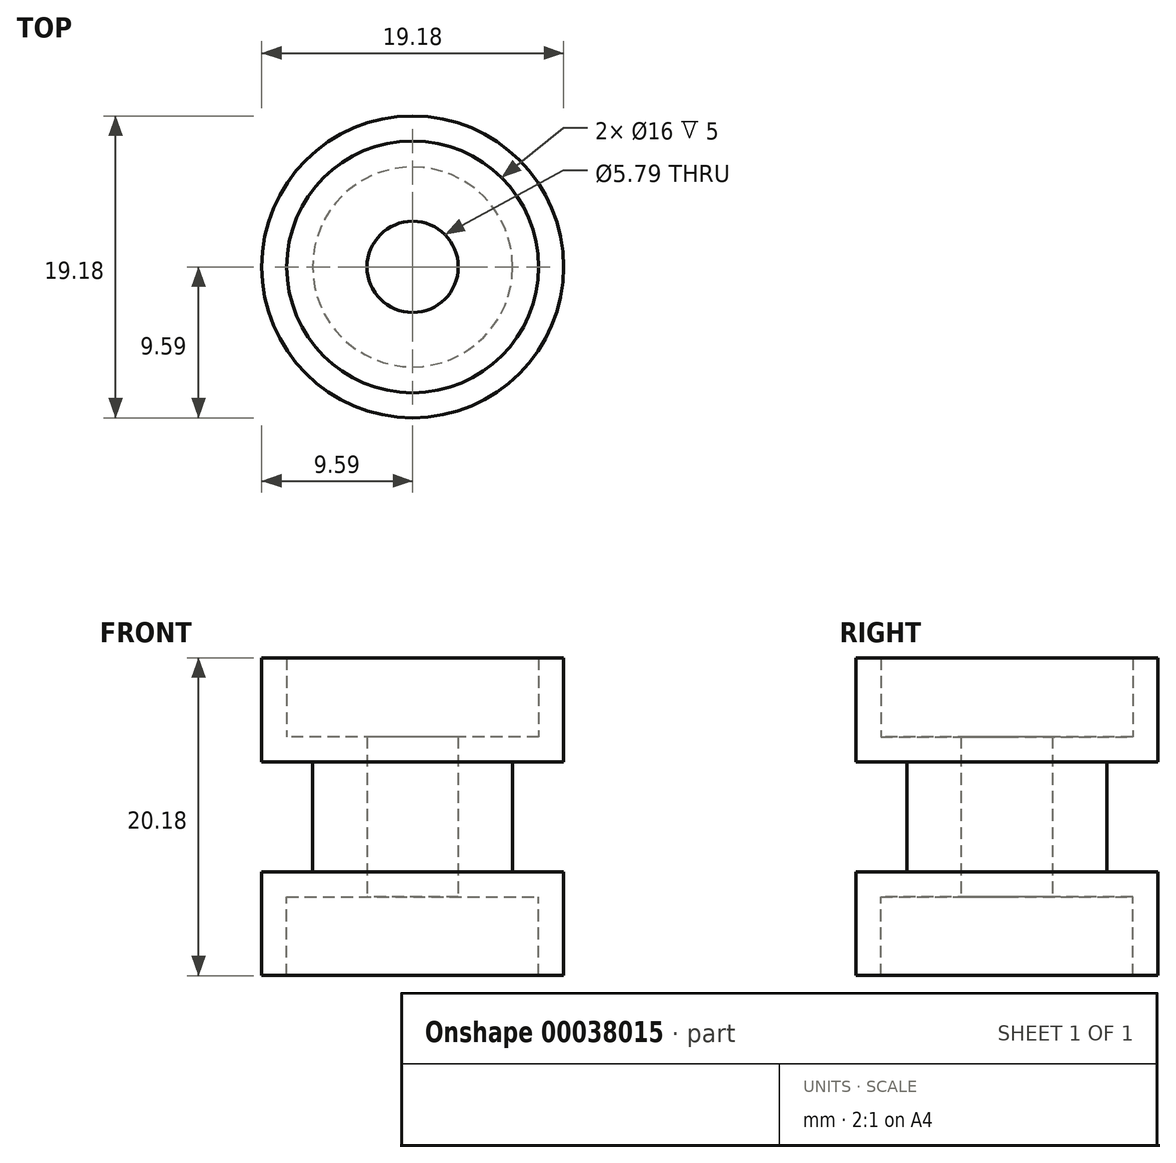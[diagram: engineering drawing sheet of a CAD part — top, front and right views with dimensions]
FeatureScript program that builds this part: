
annotation { "Feature Type Name" : "Feature", "Feature Type Description" : "" }
export const myFeature = defineFeature(function(context is Context, id is Id, definition is map)
    precondition{}
    {
        {
            var Q0;
            Q0=qCreatedBy(makeId("Top.planeOp"),FACE);
            var sketch = newSketch(context, id + "F0", { "sketchPlane" : qUnion([Q0])});
            skCircle(sketch, "E0", {"center": v(0, 0) * mm, "radius": 6.35 * mm});
            skCircle(sketch, "E1", {"center": v(0, 0) * mm, "radius": 2.9 * mm});
            skSolve(sketch);
        }
        {
            var Q0;
            Q0 = qSketchRegion(id + "F0", true);
            extrude(context, id + "F1", {"entities" : qUnion([Q0]), "depth" : 7 * mm});
        }
        {
            var Q0;
            Q0=makeQuery(id+"F1.opExtrude","CAP_FACE",FACE,{"disambiguationData":[OSD([sQuery(id+"F0.wireOp",EDGE,"E0"),sQuery(id+"F0.wireOp",EDGE,"E1")])],"isStart":false});
            var sketch = newSketch(context, id + "F2", { "sketchPlane" : qUnion([Q0])});
            skCircle(sketch, "E2", {"center": v(0, 0) * mm, "radius": 9.59 * mm});
            skCircle(sketch, "E3", {"center": v(0, 0) * mm, "radius": 2.9 * mm});
            skSolve(sketch);
        }
        {
            var Q0;
            Q0 = qSketchRegion(id + "F2", true);
            extrude(context, id + "F3", {"entities" : qUnion([Q0]), "operationType" : NewBodyOperationType.ADD, "depth" : 1.59 * mm});
        }
        {
            var Q0;
            Q0=makeQuery(id+"F3.opExtrude","CAP_FACE",FACE,{"disambiguationData":[OSD([sQuery(id+"F2.wireOp",EDGE,"E2"),sQuery(id+"F2.wireOp",EDGE,"E3")])],"isStart":false});
            var sketch = newSketch(context, id + "F4", { "sketchPlane" : qUnion([Q0])});
            skCircle(sketch, "E4", {"center": v(0, 0) * mm, "radius": 9.59 * mm});
            skCircle(sketch, "E5", {"center": v(0, 0) * mm, "radius": 8 * mm});
            skSolve(sketch);
        }
        {
            var Q0;
            Q0 = qSketchRegion(id + "F4", true);
            extrude(context, id + "F5", {"entities" : qUnion([Q0]), "operationType" : NewBodyOperationType.ADD, "depth" : 5 * mm});
        }
        {
            var Q0;
            Q0=makeQuery(id+"F1.opExtrude","CAP_FACE",FACE,{"disambiguationData":[OSD([sQuery(id+"F0.wireOp",EDGE,"E0"),sQuery(id+"F0.wireOp",EDGE,"E1")])],"isStart":true});
            var sketch = newSketch(context, id + "F6", { "sketchPlane" : qUnion([Q0])});
            skCircle(sketch, "E6", {"center": v(0, 0) * mm, "radius": 9.59 * mm});
            skCircle(sketch, "E7", {"center": v(0, 0) * mm, "radius": 2.9 * mm});
            skSolve(sketch);
        }
        {
            var Q0;
            Q0 = qSketchRegion(id + "F6", true);
            extrude(context, id + "F7", {"entities" : qUnion([Q0]), "operationType" : NewBodyOperationType.ADD, "depth" : 1.59 * mm});
        }
        {
            var Q0;
            Q0=makeQuery(id+"F7.opExtrude","CAP_FACE",FACE,{"disambiguationData":[OSD([sQuery(id+"F6.wireOp",EDGE,"E6"),sQuery(id+"F6.wireOp",EDGE,"E7")])],"isStart":false});
            var sketch = newSketch(context, id + "F8", { "sketchPlane" : qUnion([Q0])});
            skCircle(sketch, "E8", {"center": v(0, 0) * mm, "radius": 8 * mm});
            skCircle(sketch, "E9", {"center": v(0, 0) * mm, "radius": 9.59 * mm});
            skSolve(sketch);
        }
        {
            var Q0;
            Q0 = qSketchRegion(id + "F8", true);
            extrude(context, id + "F9", {"entities" : qUnion([Q0]), "operationType" : NewBodyOperationType.ADD, "depth" : 5 * mm});
        }
    });
